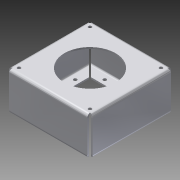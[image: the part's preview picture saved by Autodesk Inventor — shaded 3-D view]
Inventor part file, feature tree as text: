
AUTODESK INVENTOR PART (.ipt)
format: ipt  version: 2015 (Build 190159000, 159)  size: 415,232 bytes
history: native  units: in
note: dims shown in document units (in); Inventor stores cm internally (conversion verified against a paired STEP export)
features: sheet_metal_op x7, other x6, sketch x4, projected_geometry x4, hole x2
ambient origin geometry x8: Origin, YZ Plane, XZ Plane, XY Plane, X Axis, Y Axis, Z Axis, Center Point
bodies: Solid1 (feature_tree)
feature tree (23):
  sketch  "Sketch1"  dims[d4=0.133in d5=0.133in]
  sheet_metal_op  "Face1"
  hole  "Hole1"  [1 undecoded]
  sheet_metal_op  "Flange2"
  sheet_metal_op  "Flange3"
  other  "A-Side Definition"
  hole  "Hole2"  [1 undecoded]
  other  "Plate1"
  sketch  "Sketch3"  dims[d6=0.047in d7=0.047in]
  other  "Plate3"
  sheet_metal_op  "Bend2"
  sheet_metal_op  "Corner2"
  sketch  "Sketch4"  dims[d8=0.133in]
  other  "Plate4"
  sheet_metal_op  "Bend3"
  sheet_metal_op  "Corner3"
  sketch  "Sketch7"  dims[d9=0.047in d10=2.34in d11=2.34in d12=0.047in d13=0.133in d14=0.047in d15=0.133in d16=6.063in d17=6.063in d18=0.117in d19=0.25in d20=0.25in d21=0.25in d22=0.578in d23=0.25in d24=0.625in d25=0.625in d26=5.68in d27=0.25in d28=5.813in d29=5.813in d30=5.766in d31=0.625in d32=5.813in d33=5.813in d34=0.6915in d35=3.0315in d36=3.0315in d37=3.0315in d38=0.203in d39=5.438in d40=0.25in d41=0.25in d42=0.117in d43=5.813in d44=0.25in d45=0.25in d46=5.391in d47=5.813in d48=5.438in d49=5.438in d50=5.68in d51=5.813in d52=5.813in d53=5.813in d54=4.0in d55=0.125in d56=0.125in d57=0.0in d58=0.25in d59=0.75in d60=0.375in d61=0.25in d62=0.5635in d63=0.125in d64=0.8108in d75=0.125in d76=0.0625in d77=0.25in d78=0.125in d79=3.0in d80=90.0deg d81=0.125in d82=0.5in d83=0.125in d84=0.125in d85=0.3937in d86=0.125in d87=0.0625in d88=0.25in d89=0.125in d90=1.0in d91=90.0deg d92=0.125in d93=0.5in d94=0.125in d95=0.125in d96=0.75in d97=0.75in d98=0.75in d99=0.75in d100=0.25in d101=0.25in d102=0.25in d103=0.25in d104=0.25in d105=2.5681in d106=0.375in d107=0.7874in d109=1.5in d110=0.7874in d112=1.5in d115=0.7874in d117=1.5in d118=0.7874in d120=1.5in d123=0.7874in d125=1.5in d126=0.7874in d128=1.5in d131=0.7874in d133=1.5in d134=0.7874in d136=1.5in d139=0.266in d140=0.75in d141=0.507in d142=0.25in d143=0.5635in d144=0.125in d145=0.8108in]
  projected_geometry  "Projected Loop5"
  projected_geometry  "Projected Loop6"
  projected_geometry  "Projected Loop7"
  projected_geometry  "Projected Loop8"
  other  "Cut1"
  other  "Definition1"
note: 2 required parameter values undecoded (feature->parameter linkage not recoverable at this tier; creation-order binding heuristic only, values carry confidence <= 0.55)
